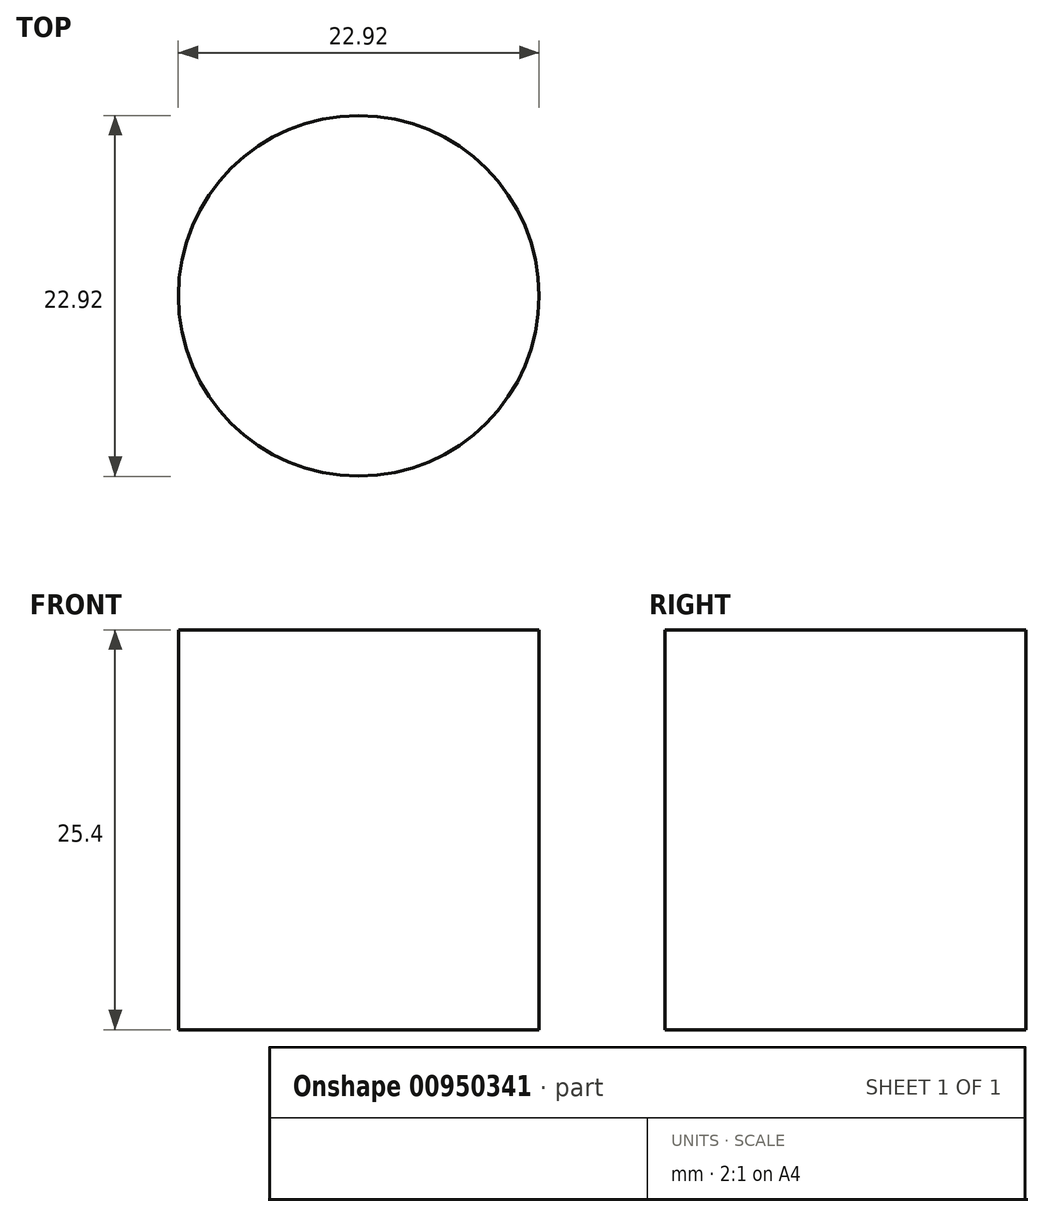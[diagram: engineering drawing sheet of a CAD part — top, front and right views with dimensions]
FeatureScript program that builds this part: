
annotation { "Feature Type Name" : "Feature", "Feature Type Description" : "" }
export const myFeature = defineFeature(function(context is Context, id is Id, definition is map)
    precondition{}
    {
        {
            var Q0;
            Q0=qCreatedBy(makeId("Top.planeOp"),FACE);
            var sketch = newSketch(context, id + "F0", { "sketchPlane" : qUnion([Q0])});
            skCircle(sketch, "E0", {"center": v(0, 0) * mm, "radius": 11.46 * mm});
            skSolve(sketch);
        }
        {
            var Q0;
            Q0=makeQuery(id+"F0.imprint","IMPRINT",FACE,{"disambiguationData":[TD([[makeQuery(id+"F0.imprint","IMPRINT",EDGE,{"derivedFrom":sQuery(id+"F0.wireOp",EDGE,"E0")}),1.0]])]});
            extrude(context, id + "F1", {"entities" : qUnion([Q0]), "depth" : 25.4 * mm, "offsetDistance" : 25.4 * mm});
        }
    });
